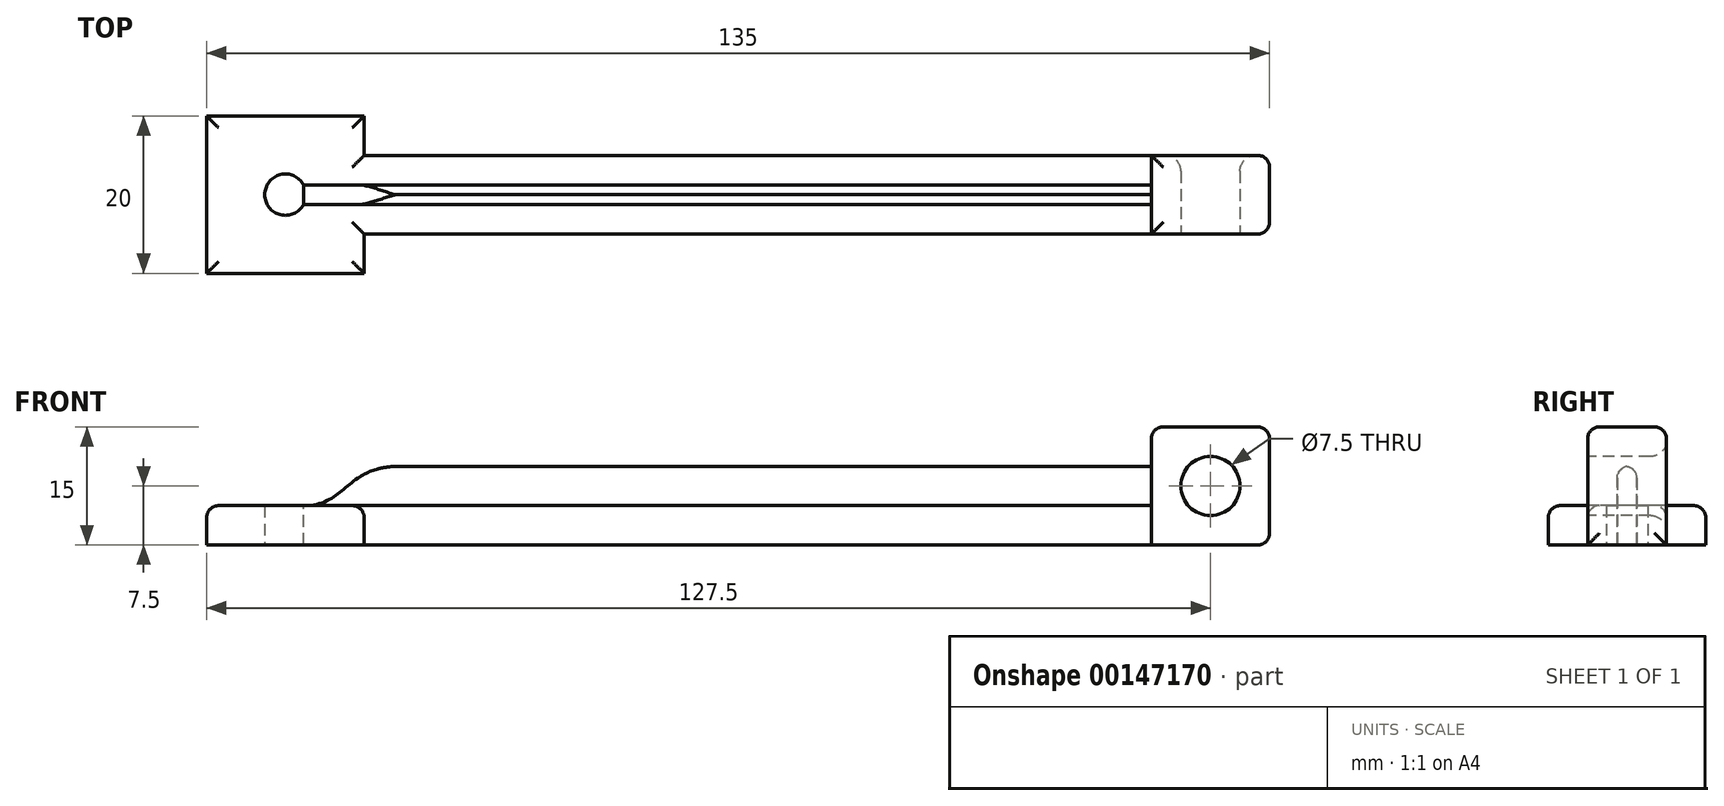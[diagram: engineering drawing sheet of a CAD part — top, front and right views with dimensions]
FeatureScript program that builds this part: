
annotation { "Feature Type Name" : "Feature", "Feature Type Description" : "" }
export const myFeature = defineFeature(function(context is Context, id is Id, definition is map)
    precondition{}
    {
        {
            var Q0;
            Q0=qCreatedBy(makeId("Top.planeOp"),FACE);
            var sketch = newSketch(context, id + "F0", { "sketchPlane" : qUnion([Q0])});
            skLineSegment(sketch, "E0.bottom", {"start": v(-10, 10) * mm, "end": v(10, 10) * mm});
            skLineSegment(sketch, "E0.top", {"start": v(-10, -10) * mm, "end": v(10, -10) * mm});
            skLineSegment(sketch, "E0.left", {"start": v(-10, 10) * mm, "end": v(-10, -10) * mm});
            skLineSegment(sketch, "E0.right", {"start": v(10, 10) * mm, "end": v(10, -10) * mm});
            skPoint(sketch, "E0.middle", {"position": v(0, 0) * mm});
            skLineSegment(sketch, "E1", {"start": v(-10, 0) * mm, "end": v(10, 0) * mm, "construction": true});
            skLineSegment(sketch, "E2", {"start": v(10, 0) * mm, "end": v(0, 10) * mm, "construction": true});
            skLineSegment(sketch, "E3", {"start": v(5, 5) * mm, "end": v(10, 5) * mm, "construction": true});
            skLineSegment(sketch, "E4", {"start": v(10, 0) * mm, "end": v(0, -10) * mm, "construction": true});
            skLineSegment(sketch, "E5", {"start": v(5, -5) * mm, "end": v(10, -5) * mm, "construction": true});
            skLineSegment(sketch, "E6.bottom", {"start": v(10, 5) * mm, "end": v(110, 5) * mm});
            skLineSegment(sketch, "E6.top", {"start": v(10, -5) * mm, "end": v(110, -5) * mm});
            skLineSegment(sketch, "E6.left", {"start": v(10, 5) * mm, "end": v(10, -5) * mm});
            skLineSegment(sketch, "E6.right", {"start": v(110, 5) * mm, "end": v(110, -5) * mm});
            skLineSegment(sketch, "E7.bottom", {"start": v(110, 5) * mm, "end": v(125, 5) * mm});
            skLineSegment(sketch, "E7.top", {"start": v(110, -5) * mm, "end": v(125, -5) * mm});
            skLineSegment(sketch, "E7.right", {"start": v(125, 5) * mm, "end": v(125, -5) * mm});
            skLineSegment(sketch, "E8.left", {"start": v(2.1, 5.96) * mm, "end": v(0.24, 1.78) * mm, "construction": true});
            skLineSegment(sketch, "E9.left", {"start": v(0, 78.73) * mm, "end": v(-26.7, 68.72) * mm});
            skCircle(sketch, "E10", {"center": v(0, 0) * mm, "radius": 2.62 * mm});
            skLineSegment(sketch, "E11.bottom", {"start": v(0, 1.25) * mm, "end": v(110, 1.25) * mm});
            skLineSegment(sketch, "E11.top", {"start": v(0, -1.25) * mm, "end": v(110, -1.25) * mm});
            skLineSegment(sketch, "E11.left", {"start": v(0, 1.25) * mm, "end": v(0, -1.25) * mm});
            skLineSegment(sketch, "E11.right", {"start": v(110, 1.25) * mm, "end": v(110, -1.25) * mm});
            skSolve(sketch);
        }
        {
            var Q0;
            {var subQ1=sQuery(id+"F0.wireOp",EDGE,"E0.bottom");Q0=makeQuery(id+"F0.imprint","IMPRINT",FACE,{"disambiguationData":[TD([[makeQuery(id+"F0.imprint","IMPRINT",EDGE,{"derivedFrom":subQ1}),-1.0]])]});}
            var Q1;
            {var subQ5=sQuery(id+"F0.wireOp",EDGE,"E6.bottom");Q1=makeQuery(id+"F0.imprint","IMPRINT",FACE,{"disambiguationData":[TD([[makeQuery(id+"F0.imprint","IMPRINT",EDGE,{"derivedFrom":subQ5}),-1.0]])]});}
            var Q2;
            {var subQ4=sQuery(id+"F0.wireOp",EDGE,"E6.top");Q2=makeQuery(id+"F0.imprint","IMPRINT",FACE,{"disambiguationData":[TD([[makeQuery(id+"F0.imprint","IMPRINT",EDGE,{"derivedFrom":subQ4}),1.0]])]});}
            extrude(context, id + "F1", {"entities" : qUnion([Q0, Q1, Q2]), "depth" : 5 * mm});
        }
        {
            var Q0;
            Q0=makeQuery(id+"F0.imprint","IMPRINT",FACE,{"disambiguationData":[TD([[makeQuery(id+"F0.imprint","IMPRINT",EDGE,{"derivedFrom":sQuery(id+"F0.wireOp",EDGE,"E11.bottom")}),-1.0]])]});
            extrude(context, id + "F2", {"entities" : qUnion([Q0]), "depth" : 10 * mm});
        }
        {
            var Q0;
            {var subQ3=sQuery(id+"F0.wireOp",EDGE,"E7.bottom");Q0=makeQuery(id+"F0.imprint","IMPRINT",FACE,{"disambiguationData":[TD([[makeQuery(id+"F0.imprint","IMPRINT",EDGE,{"derivedFrom":subQ3}),-1.0]])]});}
            extrude(context, id + "F3", {"entities" : qUnion([Q0]), "depth" : 15 * mm});
        }
        {
            var Q0;
            Q0=makeQuery(id+"F3.opExtrude","SWEPT_FACE",FACE,{"disambiguationData":[OSD([sQuery(id+"F0.wireOp",EDGE,"E7.top")])]});
            var sketch = newSketch(context, id + "F4", { "sketchPlane" : qUnion([Q0])});
            skCircle(sketch, "E12", {"center": v(117.5, 7.5) * mm, "radius": 10.6 * mm});
            skPoint(sketch, "E12.centerSnap0", {"position": v(117.5, 0) * mm});
            skPoint(sketch, "E12.centerSnap1", {"position": v(110, 7.5) * mm});
            skLineSegment(sketch, "E13.0.0", {"start": v(110, 0) * mm, "end": v(125, 0) * mm});
            skLineSegment(sketch, "E13.0.1", {"start": v(125, 0) * mm, "end": v(125, 15) * mm});
            skLineSegment(sketch, "E13.0.2", {"start": v(110, 15) * mm, "end": v(110, 15) * mm});
            skLineSegment(sketch, "E13.0.3", {"start": v(110, 15) * mm, "end": v(110, 0) * mm});
            skCircle(sketch, "E14", {"center": v(117.5, 7.5) * mm, "radius": 3.75 * mm});
            skSolve(sketch);
        }
        {
            var Q0;
            Q0=makeQuery(id+"F4.imprint","IMPRINT",FACE,{"disambiguationData":[TD([[makeQuery(id+"F4.imprint","IMPRINT",EDGE,{"derivedFrom":sQuery(id+"F4.wireOp",EDGE,"E14")}),1.0]])]});
            extrude(context, id + "F5", {"entities" : qUnion([Q0]), "operationType" : NewBodyOperationType.REMOVE, "oppositeDirection" : true, "depth" : 30.02 * mm});
        }
        {
            var Q0;
            Q0=makeQuery(id+"F3.opExtrude","CAP_EDGE",EDGE,{"disambiguationData":[OSD([sQuery(id+"F0.wireOp",EDGE,"E6.right"),sQuery(id+"F0.wireOp",EDGE,"E9.right")])],"isStart":false});
            var Q1;
            Q1=makeQuery(id+"F3.opExtrude","CAP_EDGE",EDGE,{"disambiguationData":[OSD([sQuery(id+"F0.wireOp",EDGE,"E7.right")])],"isStart":false});
            var Q2;
            Q2=makeQuery(id+"F3.opExtrude","CAP_EDGE",EDGE,{"disambiguationData":[OSD([sQuery(id+"F0.wireOp",EDGE,"E7.right")])],"isStart":true});
            var Q3;
            Q3=makeQuery(id+"F3.opExtrude","CAP_EDGE",EDGE,{"disambiguationData":[OSD([sQuery(id+"F0.wireOp",EDGE,"E7.top")])],"isStart":false});
            var Q4;
            Q4=makeQuery(id+"F3.opExtrude","SWEPT_EDGE",EDGE,{"disambiguationData":[OSD([sQuery(id+"F0.wireOp",EDGE,"E7.top"),sQuery(id+"F0.wireOp",EDGE,"E7.right")])]});
            var Q5;
            Q5=makeQuery(id+"F3.opExtrude","CAP_EDGE",EDGE,{"disambiguationData":[OSD([sQuery(id+"F0.wireOp",EDGE,"E7.bottom")])],"isStart":false});
            var Q6;
            Q6=makeQuery(id+"F3.opExtrude","SWEPT_EDGE",EDGE,{"disambiguationData":[OSD([sQuery(id+"F0.wireOp",EDGE,"E7.bottom"),sQuery(id+"F0.wireOp",EDGE,"E7.right")])]});
            fillet(context, id + "F6", {"entities" : qUnion([Q0, Q1, Q2, Q3, Q4, Q5, Q6]), "radius" : 1.5 * mm, "tangentPropagation" : true, "allowEdgeOverflow" : false});
        }
        {
            var Q0;
            Q0=makeQuery(id+"F2.opExtrude","CAP_EDGE",EDGE,{"disambiguationData":[OSD([sQuery(id+"F0.wireOp",EDGE,"E9.top")])],"isStart":false});
            var Q1;
            Q1=makeQuery(id+"F2.opExtrude","CAP_EDGE",EDGE,{"disambiguationData":[OSD([sQuery(id+"F0.wireOp",EDGE,"E9.bottom")])],"isStart":false});
            var Q2;
            Q2=makeQuery(id+"F1.opExtrude","CAP_EDGE",EDGE,{"disambiguationData":[OSD([sQuery(id+"F0.wireOp",EDGE,"E6.top")])],"isStart":false});
            var Q3;
            Q3=makeQuery(id+"F1.opExtrude","CAP_EDGE",EDGE,{"disambiguationData":[OSD([sQuery(id+"F0.wireOp",EDGE,"E6.bottom")])],"isStart":false});
            var Q4;
            Q4=makeQuery(id+"F1.opExtrude","CAP_EDGE",EDGE,{"disambiguationData":[OSD([sQuery(id+"F0.wireOp",EDGE,"E0.bottom")])],"isStart":false});
            var Q5;
            {var subQ0=sQuery(id+"F0.wireOp",EDGE,"E0.right");Q5=makeQuery(id+"F1.opExtrude","CAP_EDGE",EDGE,{"disambiguationData":[OSD([subQ0]),TDD([makeQuery(id+"F0.imprint","IMPRINT",EDGE,{"disambiguationData":[TD([[makeQuery(id+"F0.imprint","INTERSECT",VERTEX,{"derivedFrom":[sQuery(id+"F0.wireOp",EDGE,"E0.bottom"),subQ0]}),-1.0]])],"derivedFrom":subQ0})])],"isStart":false});}
            var Q6;
            {var subQ0=sQuery(id+"F0.wireOp",EDGE,"E0.right");Q6=makeQuery(id+"F1.opExtrude","CAP_EDGE",EDGE,{"disambiguationData":[OSD([subQ0]),TDD([makeQuery(id+"F0.imprint","IMPRINT",EDGE,{"disambiguationData":[TD([[makeQuery(id+"F0.imprint","INTERSECT",VERTEX,{"derivedFrom":[sQuery(id+"F0.wireOp",EDGE,"E0.top"),subQ0]}),1.0]])],"derivedFrom":subQ0})])],"isStart":false});}
            var Q7;
            Q7=makeQuery(id+"F1.opExtrude","CAP_EDGE",EDGE,{"disambiguationData":[OSD([sQuery(id+"F0.wireOp",EDGE,"E0.top")])],"isStart":false});
            var Q8;
            Q8=makeQuery(id+"F1.opExtrude","CAP_EDGE",EDGE,{"disambiguationData":[OSD([sQuery(id+"F0.wireOp",EDGE,"E0.left")])],"isStart":false});
            var Q9;
            Q9=makeQuery(id+"F2.opExtrude","CAP_EDGE",EDGE,{"disambiguationData":[OSD([sQuery(id+"F0.wireOp",EDGE,"E11.top")])],"isStart":false});
            var Q10;
            Q10=makeQuery(id+"F2.opExtrude","CAP_EDGE",EDGE,{"disambiguationData":[OSD([sQuery(id+"F0.wireOp",EDGE,"E11.bottom")])],"isStart":false});
            fillet(context, id + "F7", {"entities" : qUnion([Q0, Q1, Q2, Q3, Q4, Q5, Q6, Q7, Q8, Q9, Q10]), "radius" : 1.5 * mm, "tangentPropagation" : true, "allowEdgeOverflow" : false});
        }
        {
            var Q0;
            Q0=makeQuery(id+"F2.opExtrude","SWEPT_FACE",FACE,{"disambiguationData":[OSD([sQuery(id+"F0.wireOp",EDGE,"E11.top")])]});
            var sketch = newSketch(context, id + "F8", { "sketchPlane" : qUnion([Q0])});
            skLineSegment(sketch, "E15.0", {"start": v(2.3, 5) * mm, "end": v(110, 5) * mm});
            skLineSegment(sketch, "E16", {"start": v(2.3, 5) * mm, "end": v(0, 5) * mm});
            skLineSegment(sketch, "E17.0.0", {"start": v(0, 8.5) * mm, "end": v(0, 9.98) * mm});
            skLineSegment(sketch, "E17.0.1", {"start": v(110, 8.5) * mm, "end": v(0, 8.5) * mm});
            skLineSegment(sketch, "E17.0.2", {"start": v(110, 8.5) * mm, "end": v(110, 9.98) * mm});
            skLineSegment(sketch, "E17.0.3", {"start": v(110, 9.98) * mm, "end": v(0, 9.98) * mm});
            skLineSegment(sketch, "E18.0.0", {"start": v(110, 0) * mm, "end": v(110, 8.5) * mm});
            skLineSegment(sketch, "E18.0.2", {"start": v(0, 8.5) * mm, "end": v(0, 0) * mm});
            skLineSegment(sketch, "E18.0.3", {"start": v(0, 0) * mm, "end": v(110, 0) * mm});
            skFitSpline(sketch, "E19", {"points": [v(2.3, 5) * mm, v(14.36, 9.98) * mm], "startDerivative": vector(16.34, 0) * mm, "endDerivative": vector(19.8, 0) * mm});
            skSolve(sketch);
        }
        {
            var Q0;
            {var subQ0=sQuery(id+"F8.wireOp",EDGE,"E16");Q0=makeQuery(id+"F8.imprint","IMPRINT",FACE,{"disambiguationData":[TD([[makeQuery(id+"F8.imprint","IMPRINT",EDGE,{"derivedFrom":subQ0}),-1.0]])]});}
            var Q1;
            {var subQ0=sQuery(id+"F8.wireOp",EDGE,"E17.0.0");Q1=makeQuery(id+"F8.imprint","IMPRINT",FACE,{"disambiguationData":[TD([[makeQuery(id+"F8.imprint","IMPRINT",EDGE,{"derivedFrom":subQ0}),-1.0]])]});}
            extrude(context, id + "F9", {"entities" : qUnion([Q0, Q1]), "operationType" : NewBodyOperationType.REMOVE, "oppositeDirection" : true, "depth" : 25 * mm});
        }
        {
            var Q0;
            {var subQ5=sQuery(id+"F0.wireOp",EDGE,"E11.left");Q0=makeQuery(id+"F0.imprint","IMPRINT",FACE,{"disambiguationData":[TD([[makeQuery(id+"F0.imprint","IMPRINT",EDGE,{"derivedFrom":subQ5}),-1.0]])]});}
            var Q1;
            Q1=makeQuery(id+"F9.boolean.opBoolean","COPY",FACE,{"derivedFrom":makeQuery(id+"F9.opExtrude","SWEPT_FACE",FACE,{"disambiguationData":[OSD([sQuery(id+"F8.wireOp",EDGE,"Xsfl9bUJ-CShi-Uoxw-aEfo-lC1LjiXzIiVe")])]})});
            var Q2;
            Q2=makeQuery(id+"F9.boolean.opBoolean","COPY",FACE,{"derivedFrom":makeQuery(id+"F9.opExtrude","SWEPT_FACE",FACE,{"disambiguationData":[OSD([sQuery(id+"F8.wireOp",EDGE,"E16")])]})});
            extrude(context, id + "F10", {"entities" : qUnion([Q0, Q1, Q2]), "operationType" : NewBodyOperationType.REMOVE, "oppositeDirection" : true, "depth" : 25 * mm});
        }
        {
            var Q0;
            Q0=makeQuery(id+"F5.boolean.opBoolean","COPY",EDGE,{"derivedFrom":makeQuery(id+"F5.opExtrude","CAP_EDGE",EDGE,{"disambiguationData":[OSD([sQuery(id+"F4.wireOp",EDGE,"E14")])],"isStart":true})});
            var Q1;
            Q1=makeQuery(id+"F5.boolean.opBoolean","INTERSECT",EDGE,{"derivedFrom":[makeQuery(id+"F3.opExtrude","SWEPT_FACE",FACE,{"disambiguationData":[OSD([sQuery(id+"F0.wireOp",EDGE,"E7.bottom")])]}),makeQuery(id+"F5.opExtrude","SWEPT_FACE",FACE,{"disambiguationData":[OSD([sQuery(id+"F4.wireOp",EDGE,"E14")])]})]});
            fillet(context, id + "F11", {"entities" : qUnion([Q0, Q1]), "radius" : 2 * mm, "tangentPropagation" : true, "allowEdgeOverflow" : false});
        }
    });
